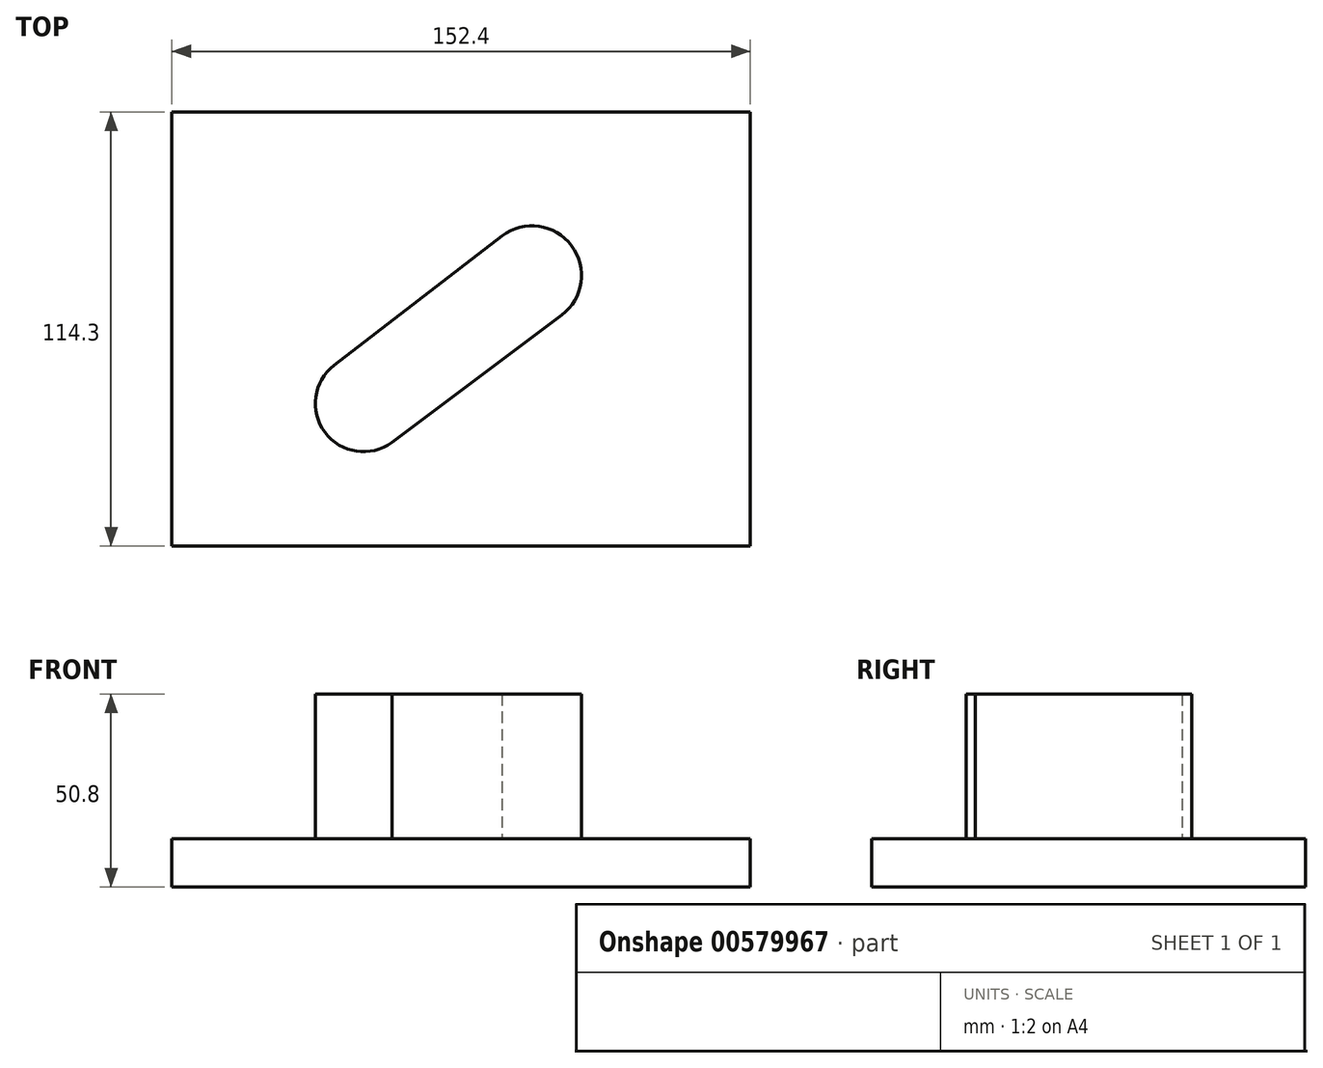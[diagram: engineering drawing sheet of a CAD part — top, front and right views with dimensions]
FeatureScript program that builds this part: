
annotation { "Feature Type Name" : "Feature", "Feature Type Description" : "" }
export const myFeature = defineFeature(function(context is Context, id is Id, definition is map)
    precondition{}
    {
        {
            var Q0;
            Q0=qCreatedBy(makeId("Top.planeOp"),FACE);
            var sketch = newSketch(context, id + "F0", { "sketchPlane" : qUnion([Q0])});
            skLineSegment(sketch, "E0.bottom", {"start": v(76.2, -57.15) * mm, "end": v(-76.2, -57.15) * mm});
            skLineSegment(sketch, "E0.top", {"start": v(76.2, 57.15) * mm, "end": v(-76.2, 57.15) * mm});
            skLineSegment(sketch, "E0.left", {"start": v(76.2, -57.15) * mm, "end": v(76.2, 57.15) * mm});
            skLineSegment(sketch, "E0.right", {"start": v(-76.2, -57.15) * mm, "end": v(-76.2, 57.15) * mm});
            skPoint(sketch, "E0.middle", {"position": v(0, 0) * mm});
            skLineSegment(sketch, "E1", {"start": v(-76.2, -57.15) * mm, "end": v(76.2, 57.15) * mm, "construction": true});
            skSolve(sketch);
        }
        {
            var Q0;
            Q0=makeQuery(id+"F0.imprint","IMPRINT",FACE,{"disambiguationData":[TD([[makeQuery(id+"F0.imprint","IMPRINT",EDGE,{"derivedFrom":sQuery(id+"F0.wireOp",EDGE,"E0.bottom")}),-1.0]])]});
            extrude(context, id + "F1", {"entities" : qUnion([Q0]), "depth" : 12.7 * mm, "offsetDistance" : 25.4 * mm});
        }
        {
            var Q0;
            Q0=makeQuery(id+"F1.opExtrude","CAP_FACE",FACE,{"disambiguationData":[OSD([sQuery(id+"F0.wireOp",EDGE,"E0.bottom"),sQuery(id+"F0.wireOp",EDGE,"E0.top"),sQuery(id+"F0.wireOp",EDGE,"E0.left"),sQuery(id+"F0.wireOp",EDGE,"E0.right")])],"isStart":false});
            var sketch = newSketch(context, id + "F2", { "sketchPlane" : qUnion([Q0])});
            skLineSegment(sketch, "E2", {"start": v(76.2, 57.15) * mm, "end": v(-76.2, -57.15) * mm, "construction": true});
            skLineSegment(sketch, "E3", {"start": v(-33.45, -9.54) * mm, "end": v(-18.21, -29.86) * mm});
            skLineSegment(sketch, "E4", {"start": v(-18.21, -29.86) * mm, "end": v(26.49, 3.66) * mm});
            skLineSegment(sketch, "E5", {"start": v(26.49, 3.66) * mm, "end": v(10.8, 24.57) * mm});
            skLineSegment(sketch, "E6", {"start": v(10.8, 24.57) * mm, "end": v(-33.45, -9.54) * mm});
            skArc(sketch, "E7", {"start": v(-33.45, -9.54) * mm, "mid": v(-35.86, -27.22) * mm, "end": v(-18.21, -29.86) * mm});
            skArc(sketch, "E8", {"start": v(26.49, 3.66) * mm, "mid": v(29.1, 21.96) * mm, "end": v(10.8, 24.57) * mm});
            skSolve(sketch);
        }
        {
            var Q0;
            Q0=makeQuery(id+"F2.imprint","IMPRINT",FACE,{"disambiguationData":[TD([[makeQuery(id+"F2.imprint","IMPRINT",EDGE,{"derivedFrom":sQuery(id+"F2.wireOp",EDGE,"E5")}),-1.0]])]});
            var Q1;
            Q1=makeQuery(id+"F2.imprint","IMPRINT",FACE,{"disambiguationData":[TD([[makeQuery(id+"F2.imprint","IMPRINT",EDGE,{"derivedFrom":sQuery(id+"F2.wireOp",EDGE,"E3")}),1.0]])]});
            var Q2;
            Q2=makeQuery(id+"F2.imprint","IMPRINT",FACE,{"disambiguationData":[TD([[makeQuery(id+"F2.imprint","IMPRINT",EDGE,{"derivedFrom":sQuery(id+"F2.wireOp",EDGE,"E3")}),-1.0]])]});
            extrude(context, id + "F3", {"entities" : qUnion([Q0, Q1, Q2]), "operationType" : NewBodyOperationType.ADD, "depth" : 38.1 * mm, "offsetDistance" : 25.4 * mm});
        }
    });
